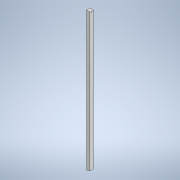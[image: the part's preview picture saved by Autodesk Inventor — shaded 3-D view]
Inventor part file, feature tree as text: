
AUTODESK INVENTOR PART (.ipt)
format: ipt  version: 2022 (Build 260153000, 153)  size: 115,200 bytes
history: native  units: mm
features: extrude x3, sketch x3
ambient origin geometry x8: Origin, YZ Plane, XZ Plane, XY Plane, X Axis, Y Axis, Z Axis, Center Point
bodies: Solid1 (feature_tree)
feature tree (6):
  extrude  "Extrusion1"  Depth=5.0mm
  extrude  "Extrusion3"  Depth=2.5mm
  extrude  "Extrusion4"  Depth=200.0mm
  sketch  "Sketch1"  dims[d0=5.0mm d1=5.0mm]
  sketch  "Sketch3"  dims[d2=2.5mm d3=2.5mm]
  sketch  "Sketch4"  dims[d4=200.0mm d5=0.0mm d9=0.75mm d10=2.0mm d11=2.5mm d12=200.0mm d13=0.0mm d14=15.0deg d15=200.0mm d16=0.0mm]
